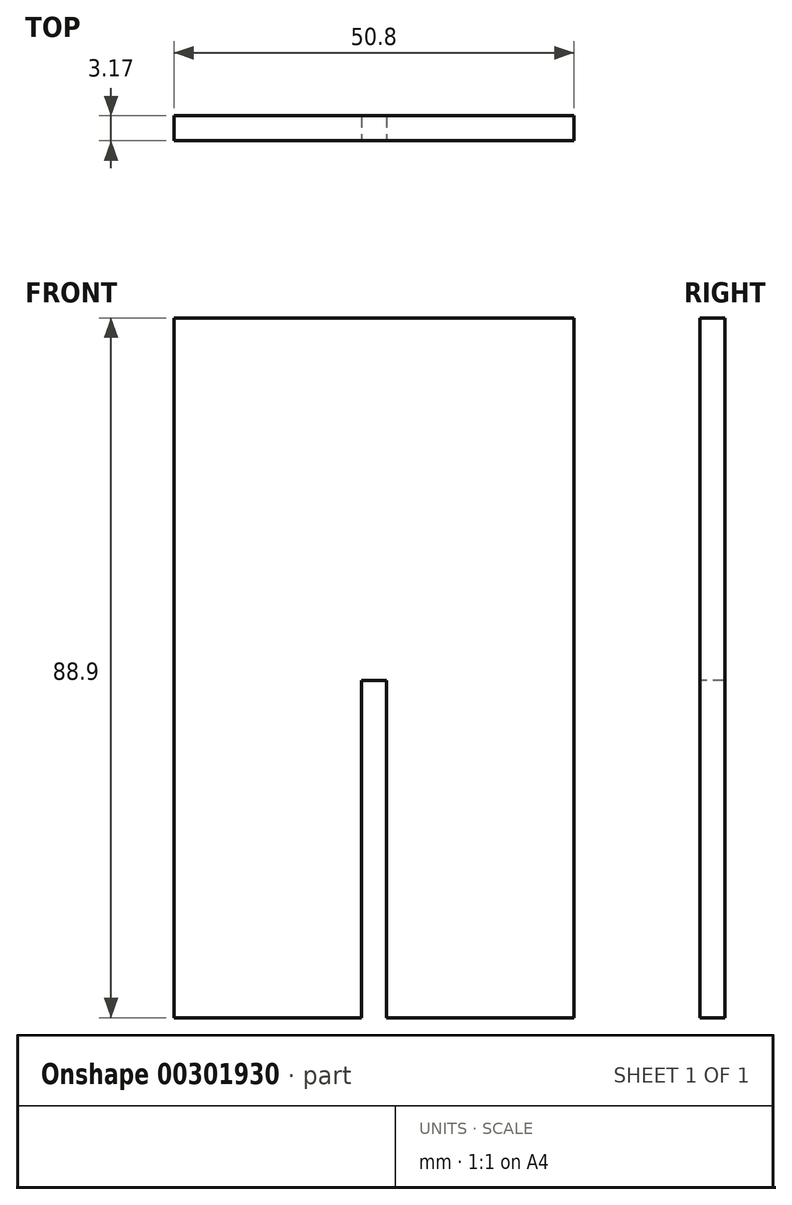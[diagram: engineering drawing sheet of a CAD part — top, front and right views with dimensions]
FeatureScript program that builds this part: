
annotation { "Feature Type Name" : "Feature", "Feature Type Description" : "" }
export const myFeature = defineFeature(function(context is Context, id is Id, definition is map)
    precondition{}
    {
        {
            var Q0;
            Q0=qCreatedBy(makeId("Front.planeOp"),FACE);
            var sketch = newSketch(context, id + "F0", { "sketchPlane" : qUnion([Q0])});
            skLineSegment(sketch, "E0.bottom", {"start": v(-25.4, 44.45) * mm, "end": v(25.4, 44.45) * mm});
            skLineSegment(sketch, "E0.top", {"start": v(-25.4, -44.45) * mm, "end": v(25.4, -44.45) * mm});
            skLineSegment(sketch, "E0.left", {"start": v(-25.4, 44.45) * mm, "end": v(-25.4, -44.45) * mm});
            skLineSegment(sketch, "E0.right", {"start": v(25.4, 44.45) * mm, "end": v(25.4, -44.45) * mm});
            skPoint(sketch, "E0.middle", {"position": v(0, 0) * mm});
            skSolve(sketch);
        }
        {
            var Q0;
            Q0=makeQuery(id+"F0.imprint","IMPRINT",FACE,{"disambiguationData":[TD([[makeQuery(id+"F0.imprint","IMPRINT",EDGE,{"derivedFrom":sQuery(id+"F0.wireOp",EDGE,"E0.bottom")}),-1.0]])]});
            extrude(context, id + "F1", {"entities" : qUnion([Q0]), "depth" : 3.17 * mm});
        }
        {
            var Q0;
            Q0=makeQuery(id+"F1.opExtrude","CAP_FACE",FACE,{"disambiguationData":[OSD([sQuery(id+"F0.wireOp",EDGE,"E0.bottom"),sQuery(id+"F0.wireOp",EDGE,"E0.top"),sQuery(id+"F0.wireOp",EDGE,"E0.left"),sQuery(id+"F0.wireOp",EDGE,"E0.right")])],"isStart":false});
            var sketch = newSketch(context, id + "F2", { "sketchPlane" : qUnion([Q0])});
            skLineSegment(sketch, "E1.bottom", {"start": v(-1.59, -44.45) * mm, "end": v(1.59, -44.45) * mm});
            skLineSegment(sketch, "E1.top", {"start": v(-1.59, -1.59) * mm, "end": v(1.59, -1.59) * mm});
            skLineSegment(sketch, "E1.left", {"start": v(-1.59, -44.45) * mm, "end": v(-1.59, -1.59) * mm});
            skLineSegment(sketch, "E1.right", {"start": v(1.59, -44.45) * mm, "end": v(1.59, -1.59) * mm});
            skSolve(sketch);
        }
        {
            var Q0;
            Q0=makeQuery(id+"F2.imprint","IMPRINT",FACE,{"disambiguationData":[TD([[makeQuery(id+"F2.imprint","IMPRINT",EDGE,{"derivedFrom":sQuery(id+"F2.wireOp",EDGE,"E1.bottom")}),1.0]])]});
            extrude(context, id + "F3", {"entities" : qUnion([Q0]), "operationType" : NewBodyOperationType.REMOVE, "endBound" : BoundingType.THROUGH_ALL, "oppositeDirection" : true, "depth" : 25.4 * mm});
        }
    });
